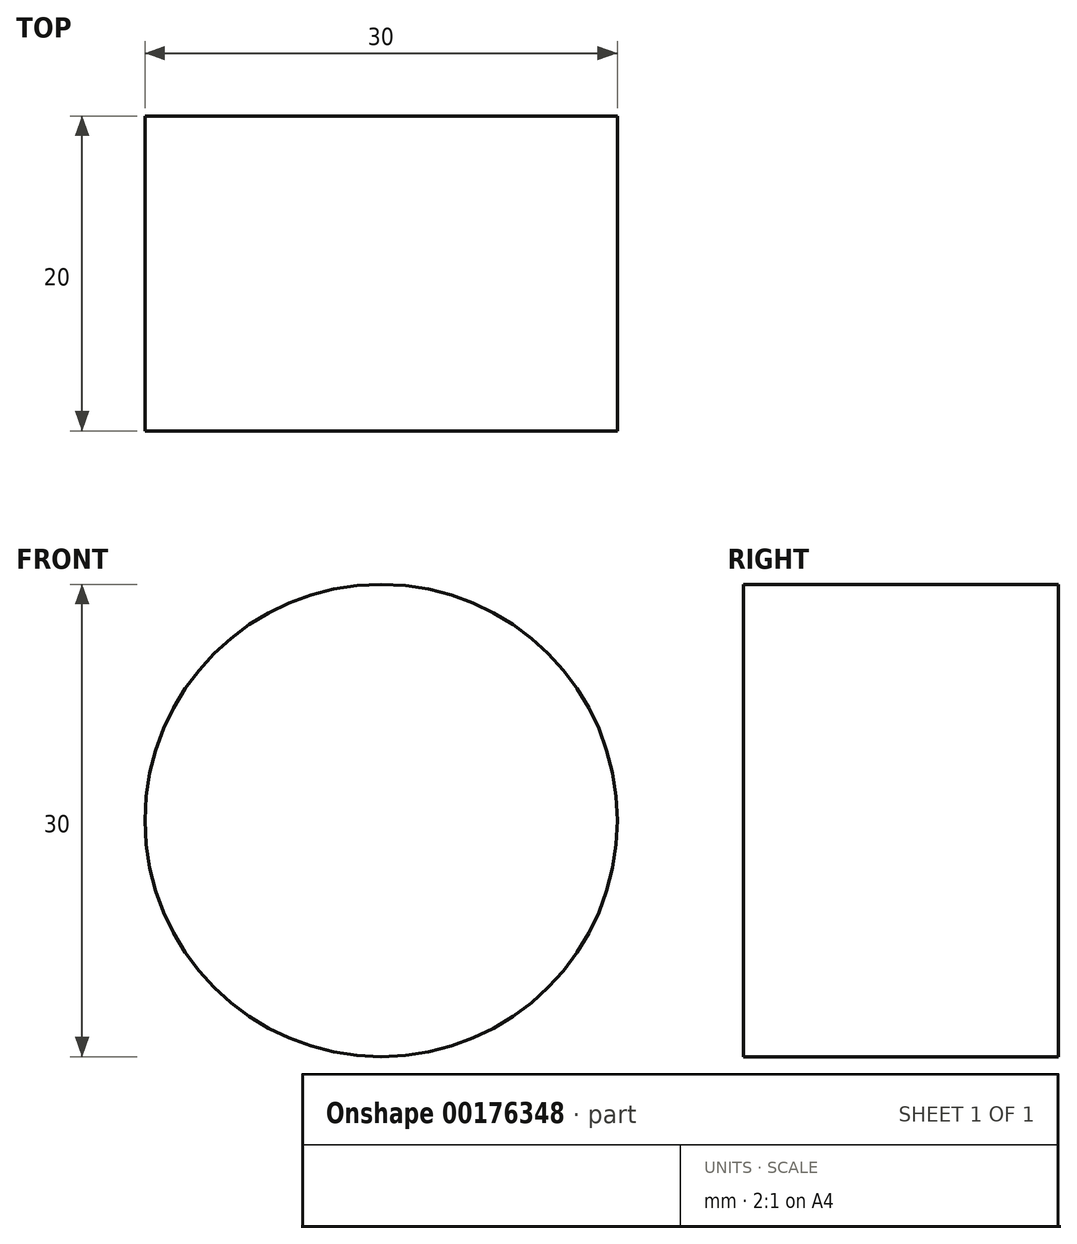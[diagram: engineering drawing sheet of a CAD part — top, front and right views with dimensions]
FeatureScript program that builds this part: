
annotation { "Feature Type Name" : "Feature", "Feature Type Description" : "" }
export const myFeature = defineFeature(function(context is Context, id is Id, definition is map)
    precondition{}
    {
        {
            var Q0;
            Q0=qCreatedBy(makeId("Front.planeOp"),FACE);
            var sketch = newSketch(context, id + "F0", { "sketchPlane" : qUnion([Q0])});
            skCircle(sketch, "E0", {"center": v(0, 0) * mm, "radius": 15 * mm});
            skSolve(sketch);
        }
        {
            var Q0;
            Q0=makeQuery(id+"F0.imprint","IMPRINT",FACE,{"disambiguationData":[TD([[makeQuery(id+"F0.imprint","IMPRINT",EDGE,{"derivedFrom":sQuery(id+"F0.wireOp",EDGE,"E0")}),1.0]])]});
            extrude(context, id + "F1", {"entities" : qUnion([Q0]), "oppositeDirection" : true, "depth" : 20 * mm});
        }
    });
